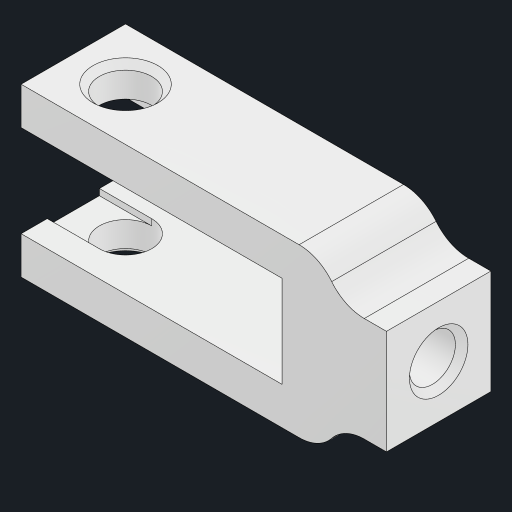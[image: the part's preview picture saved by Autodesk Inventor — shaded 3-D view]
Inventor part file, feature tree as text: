
AUTODESK INVENTOR PART (.ipt)
format: ipt  version: 2023 (Build 270158000, 158)  size: 191,488 bytes
history: native  units: mm
features: sketch x5, extrude x4, fillet x2, chamfer x2, other x1, hole x1
ambient origin geometry x8: Origin, YZ Plane, XZ Plane, XY Plane, X Axis, Y Axis, Z Axis, Center Point
bodies: Body1 (feature_tree)
feature tree (15):
  other  "ソリッド1"
  extrude  "押し出し1"  Depth=2.5mm
  extrude  "押し出し5"  Depth=2.5mm
  extrude  "押し出し3"  Depth=12.0mm
  extrude  "押し出し4"  Depth=8.0mm TaperAngle=0.0deg
  hole  "穴3"  [1 undecoded]
  fillet  "フィレット2"  Radius=3.0mm
  chamfer  "面取り1"  Distance=2.0mm
  chamfer  "面取り2"  Distance=5.0mm
  fillet  "フィレット4"  Radius=3.0mm
  sketch  "スケッチ1"
  sketch  "スケッチ3"
  sketch  "スケッチ5"
  sketch  "スケッチ7"
  sketch  "スケッチ8"
note: 1 required parameter value undecoded (feature->parameter linkage not recoverable at this tier; creation-order binding heuristic only, values carry confidence <= 0.55)
